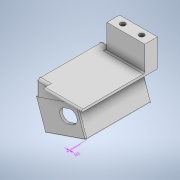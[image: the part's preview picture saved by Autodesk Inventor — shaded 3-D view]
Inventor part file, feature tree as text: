
AUTODESK INVENTOR PART (.ipt)
format: ipt  version: 2020 (Build 240168000, 168)  size: 221,696 bytes
history: native  units: in
note: dims shown in document units (in); Inventor stores cm internally (conversion verified against a paired STEP export)
features: other x5, fillet x4, extrude x1, sketch x1
ambient origin geometry x8: Origin, YZ Plane, XZ Plane, XY Plane, X Axis, Y Axis, Z Axis, Center Point
bodies: Solid1 (feature_tree), Solid2 (feature_tree)
feature tree (11):
  other  "GoPro.iam"
  other  "GoProCase.ipt:1"
  other  "Base.ipt:1"
  other  "Annotations"
  fillet  "Fillet1"  Radius=0.3937in
  extrude  "Extrusion1"  Depth=0.1in
  fillet  "Fillet2"  Radius=1.0in
  fillet  "Fillet3"  Radius=0.1in
  fillet  "Fillet4"  Radius=0.1in
  sketch  "Sketch1"  dims[d1=0.05in d2=0.1in d3=1.0in d4=0.0in d5=0.1in d6=0.1in d9=0.04in d7=0.1708in d8=0.0308in]
  other  "Linear Dimension 1"
